# Revit family: P4625-09 9-100W MED CHANDELIER
name_source: partatom
category: Lighting Fixtures
revit_build: Autodesk Revit Architecture 2012 (Build: 20110309_2315(x64)
units: mm (PartAtom-declared; Revit-internal decimal feet)

## types (1)
- P4625-09 9-100W MED CHANDELIER
    Back plate = Brushed Nickel
    Ceiling Chain Length = 65"
    Default Elevation = 48"
    Description = Nine-light chandelier with white etched glass from the Bravo collection. Linear elements stream throughout the fixture to compose a relaxed but exotic ambiance. Generously scaled glass shades add distinction against the Brushed Nickel finish and provide pleasing illumination to your room. Six feet of 9 gauge chain is supplied for ceiling chain mount. Bravo possesses a smart simplicity to complement today's home entirely with confidence and style.
    Glass = Etched Glass
    Lamp = Nine
    Manufacturer = Progress Lighting
    Manufacturer Fax = (864)-678-1065
    Model = P4625-09
    Product Documentation Link = http://www.progresslighting.com
    Product Page URL = http://www.progresslighting.com
    Wattage = 150 W

## geometry (parser evidence)
native form markers: Blend x1, Sweep x12
no freeform markers — native parametric forms only
